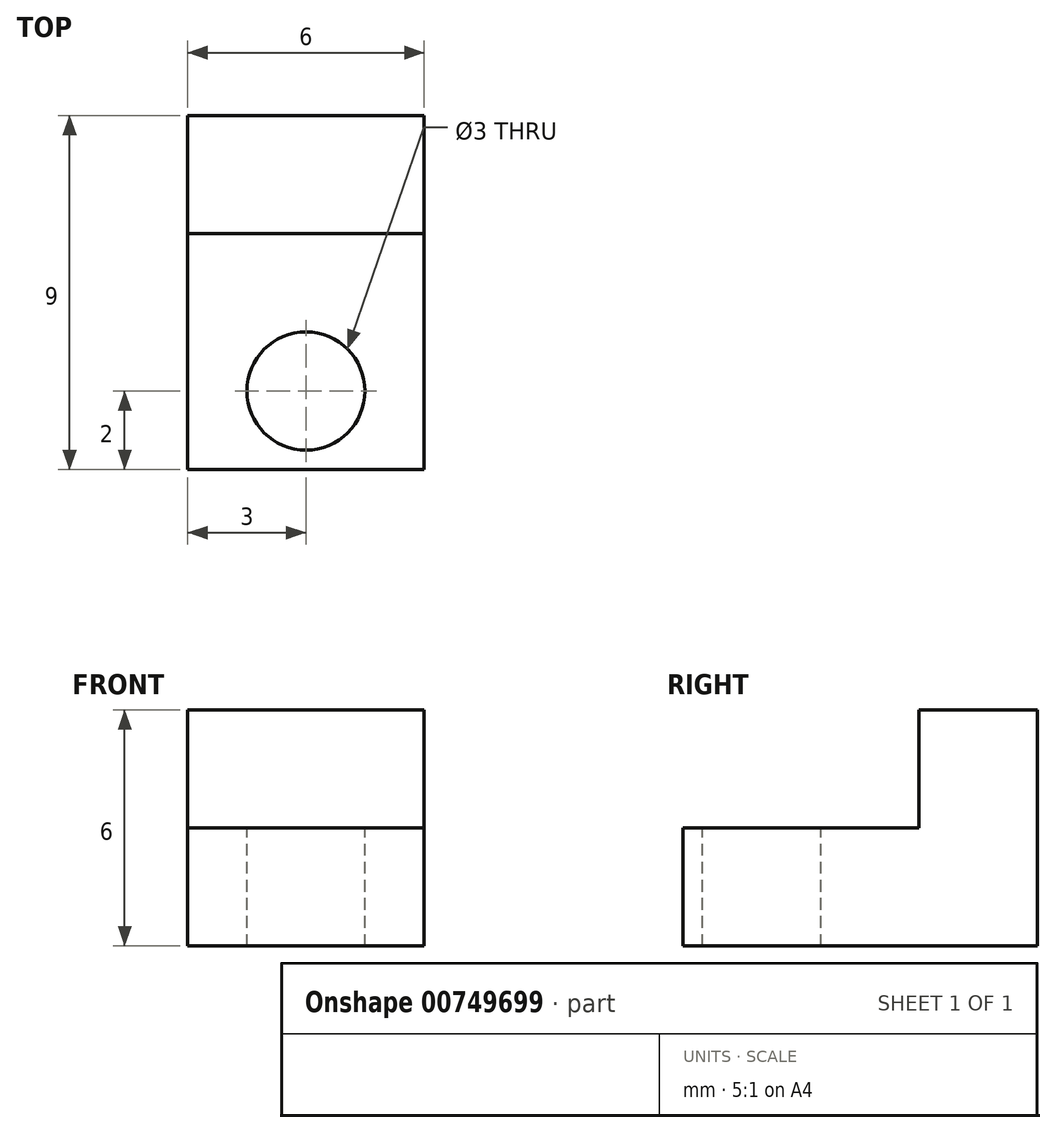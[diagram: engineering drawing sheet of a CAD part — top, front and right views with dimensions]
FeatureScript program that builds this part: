
annotation { "Feature Type Name" : "Feature", "Feature Type Description" : "" }
export const myFeature = defineFeature(function(context is Context, id is Id, definition is map)
    precondition{}
    {
        {
            var Q0;
            Q0=qCreatedBy(makeId("Right.planeOp"),FACE);
            var sketch = newSketch(context, id + "F0", { "sketchPlane" : qUnion([Q0])});
            skLineSegment(sketch, "E0", {"start": v(0, 0) * mm, "end": v(-9, 0) * mm});
            skLineSegment(sketch, "E1", {"start": v(-9, 0) * mm, "end": v(-9, 3) * mm});
            skLineSegment(sketch, "E2", {"start": v(-9, 3) * mm, "end": v(-3, 3) * mm});
            skLineSegment(sketch, "E3", {"start": v(-3, 3) * mm, "end": v(-3, 6) * mm});
            skLineSegment(sketch, "E4", {"start": v(-3, 6) * mm, "end": v(0, 6) * mm});
            skLineSegment(sketch, "E5", {"start": v(0, 6) * mm, "end": v(0, 0) * mm});
            skSolve(sketch);
        }
        {
            var Q0;
            Q0=makeQuery(id+"F0.imprint","IMPRINT",FACE,{"disambiguationData":[TD([[makeQuery(id+"F0.imprint","IMPRINT",EDGE,{"derivedFrom":sQuery(id+"F0.wireOp",EDGE,"E0")}),-1.0]])]});
            extrude(context, id + "F1", {"entities" : qUnion([Q0]), "depth" : 6 * mm, "offsetDistance" : 25 * mm});
        }
        {
            var Q0;
            Q0=makeQuery(id+"F1.opExtrude","SWEPT_FACE",FACE,{"disambiguationData":[OSD([sQuery(id+"F0.wireOp",EDGE,"E2")])]});
            var sketch = newSketch(context, id + "F2", { "sketchPlane" : qUnion([Q0])});
            skLineSegment(sketch, "E6", {"start": v(0, -9) * mm, "end": v(0, -7) * mm, "construction": true});
            skLineSegment(sketch, "E7", {"start": v(0, -7) * mm, "end": v(3, -7) * mm, "construction": true});
            skPoint(sketch, "E7.endSnap0", {"position": v(3, -9) * mm});
            skCircle(sketch, "E8", {"center": v(3, -7) * mm, "radius": 1.5 * mm});
            skSolve(sketch);
        }
        {
            var Q0;
            Q0=makeQuery(id+"F2.imprint","IMPRINT",FACE,{"disambiguationData":[TD([[makeQuery(id+"F2.imprint","IMPRINT",EDGE,{"derivedFrom":sQuery(id+"F2.wireOp",EDGE,"E8")}),1.0]])]});
            extrude(context, id + "F3", {"entities" : qUnion([Q0]), "operationType" : NewBodyOperationType.REMOVE, "oppositeDirection" : true, "depth" : 25 * mm, "offsetDistance" : 25 * mm});
        }
    });
